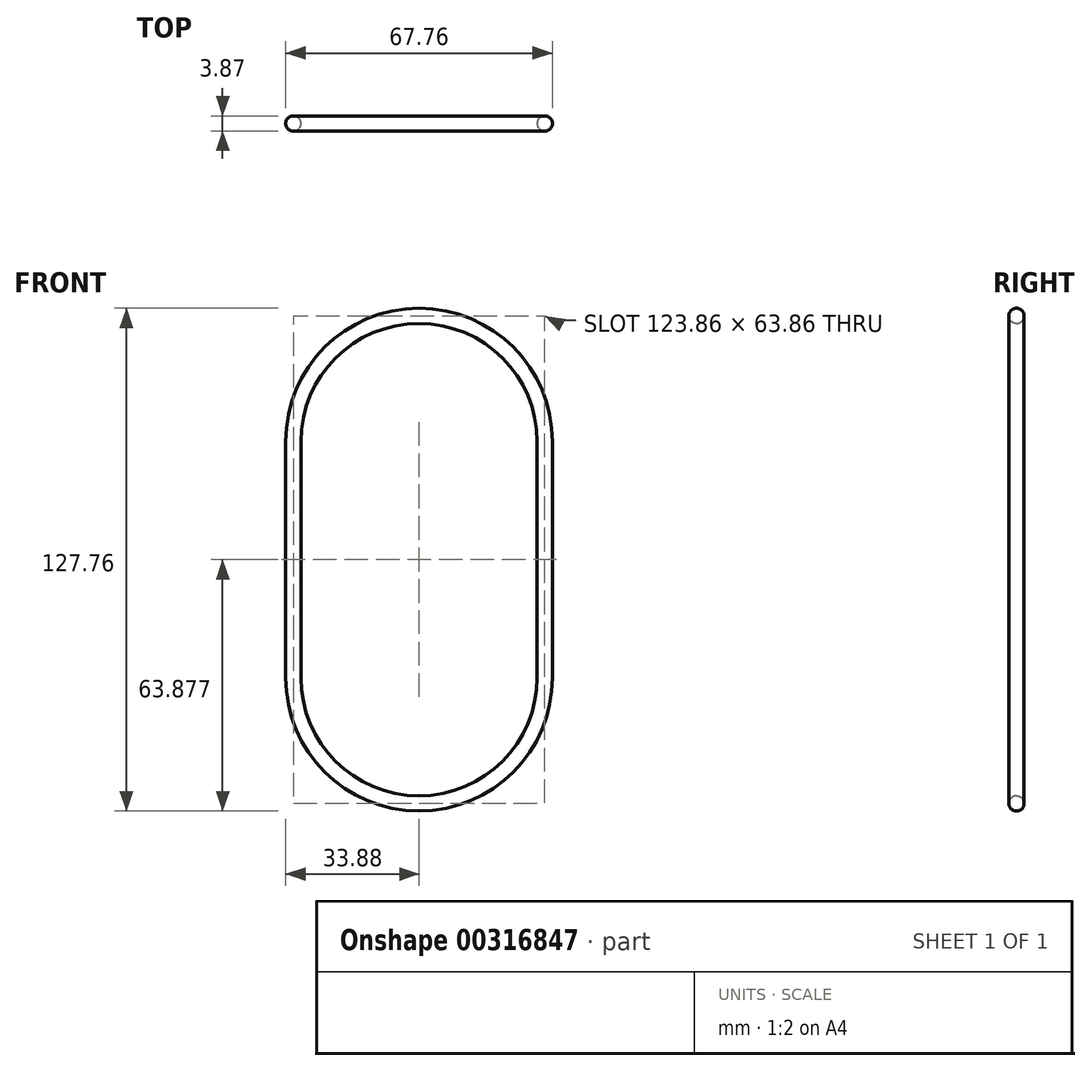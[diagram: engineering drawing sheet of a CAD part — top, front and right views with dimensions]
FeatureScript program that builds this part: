
annotation { "Feature Type Name" : "Feature", "Feature Type Description" : "" }
export const myFeature = defineFeature(function(context is Context, id is Id, definition is map)
    precondition{}
    {
        {
            var Q0;
            Q0=qCreatedBy(makeId("Front.planeOp"),FACE);
            var sketch = newSketch(context, id + "F0", { "sketchPlane" : qUnion([Q0])});
            skLineSegment(sketch, "E0", {"start": v(-30, 29.7) * mm, "end": v(-30, -30.3) * mm});
            skLineSegment(sketch, "E1.MirrorCS", {"start": v(30, 29.7) * mm, "end": v(30, -30.3) * mm});
            skArc(sketch, "E2", {"start": v(30, 29.7) * mm, "mid": v(0, 59.7) * mm, "end": v(-30, 29.7) * mm});
            skArc(sketch, "E3", {"start": v(-30, -30.3) * mm, "mid": v(0, -60.3) * mm, "end": v(30, -30.3) * mm});
            skLineSegment(sketch, "E4", {"start": v(-33.88, 29.7) * mm, "end": v(-33.88, -30.3) * mm});
            skLineSegment(sketch, "E5", {"start": v(33.88, -30.3) * mm, "end": v(33.88, 29.7) * mm});
            skArc(sketch, "E6", {"start": v(33.88, 29.7) * mm, "mid": v(0, 63.58) * mm, "end": v(-33.88, 29.7) * mm});
            skArc(sketch, "E7", {"start": v(-33.88, -30.3) * mm, "mid": v(0, -64.18) * mm, "end": v(33.88, -30.3) * mm});
            skSolve(sketch);
        }
        {
            var Q0;
            Q0=makeQuery(id+"F0.imprint","IMPRINT",FACE,{"disambiguationData":[TD([[makeQuery(id+"F0.imprint","IMPRINT",EDGE,{"derivedFrom":sQuery(id+"F0.wireOp",EDGE,"E0")}),-1.0]])]});
            extrude(context, id + "F1", {"entities" : qUnion([Q0]), "depth" : 3.87 * mm});
        }
        {
            var Q0;
            Q0=makeQuery(id+"F1.opExtrude","CAP_FACE",FACE,{"disambiguationData":[OSD([sQuery(id+"F0.wireOp",EDGE,"E0"),sQuery(id+"F0.wireOp",EDGE,"E1.MirrorCS"),sQuery(id+"F0.wireOp",EDGE,"E2"),sQuery(id+"F0.wireOp",EDGE,"E3"),sQuery(id+"F0.wireOp",EDGE,"E4"),sQuery(id+"F0.wireOp",EDGE,"E5"),sQuery(id+"F0.wireOp",EDGE,"E6"),sQuery(id+"F0.wireOp",EDGE,"E7")])],"isStart":true});
            var Q1;
            Q1=makeQuery(id+"F1.opExtrude","CAP_FACE",FACE,{"disambiguationData":[OSD([sQuery(id+"F0.wireOp",EDGE,"E0"),sQuery(id+"F0.wireOp",EDGE,"E1.MirrorCS"),sQuery(id+"F0.wireOp",EDGE,"E2"),sQuery(id+"F0.wireOp",EDGE,"E3"),sQuery(id+"F0.wireOp",EDGE,"E4"),sQuery(id+"F0.wireOp",EDGE,"E5"),sQuery(id+"F0.wireOp",EDGE,"E6"),sQuery(id+"F0.wireOp",EDGE,"E7")])],"isStart":false});
            fillet(context, id + "F2", {"entities" : qUnion([Q0, Q1]), "radius" : 1.93 * mm, "tangentPropagation" : true, "allowEdgeOverflow" : false});
        }
    });
